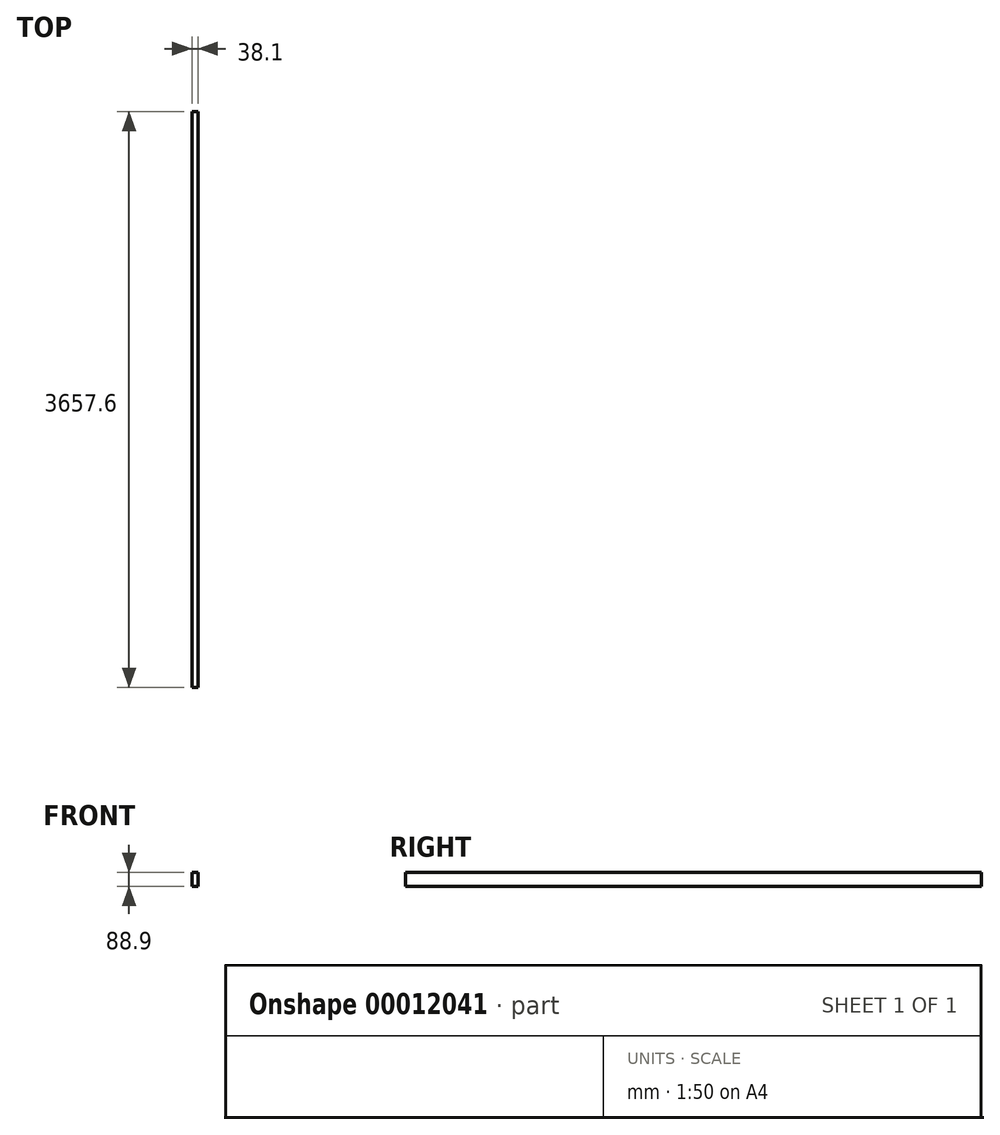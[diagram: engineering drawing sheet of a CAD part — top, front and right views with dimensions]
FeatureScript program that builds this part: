
annotation { "Feature Type Name" : "Feature", "Feature Type Description" : "" }
export const myFeature = defineFeature(function(context is Context, id is Id, definition is map)
    precondition{}
    {
        {
            var Q0;
            Q0=qCreatedBy(makeId("Front.planeOp"),FACE);
            var sketch = newSketch(context, id + "F0", { "sketchPlane" : qUnion([Q0])});
            skLineSegment(sketch, "E0.rect.bottom", {"start": v(19.05, 44.45) * mm, "end": v(-19.05, 44.45) * mm});
            skLineSegment(sketch, "E0.rect.top", {"start": v(19.05, -44.45) * mm, "end": v(-19.05, -44.45) * mm});
            skLineSegment(sketch, "E0.rect.left", {"start": v(19.05, 44.45) * mm, "end": v(19.05, -44.45) * mm});
            skLineSegment(sketch, "E0.rect.right", {"start": v(-19.05, 44.45) * mm, "end": v(-19.05, -44.45) * mm});
            skPoint(sketch, "E0.rect.middle", {"position": v(0, 0) * mm});
            skSolve(sketch);
        }
        {
            var Q0;
            Q0=makeQuery(id+"F0.imprint","IMPRINT",FACE,{"disambiguationData":[TD([[makeQuery(id+"F0.imprint","IMPRINT",EDGE,{"derivedFrom":sQuery(id+"F0.wireOp",EDGE,"E0.rect.bottom")}),1.0]])]});
            extrude(context, id + "F1", {"entities" : qUnion([Q0]), "endBound" : BoundingType.SYMMETRIC, "depth" : 3657.6 * mm});
        }
    });
